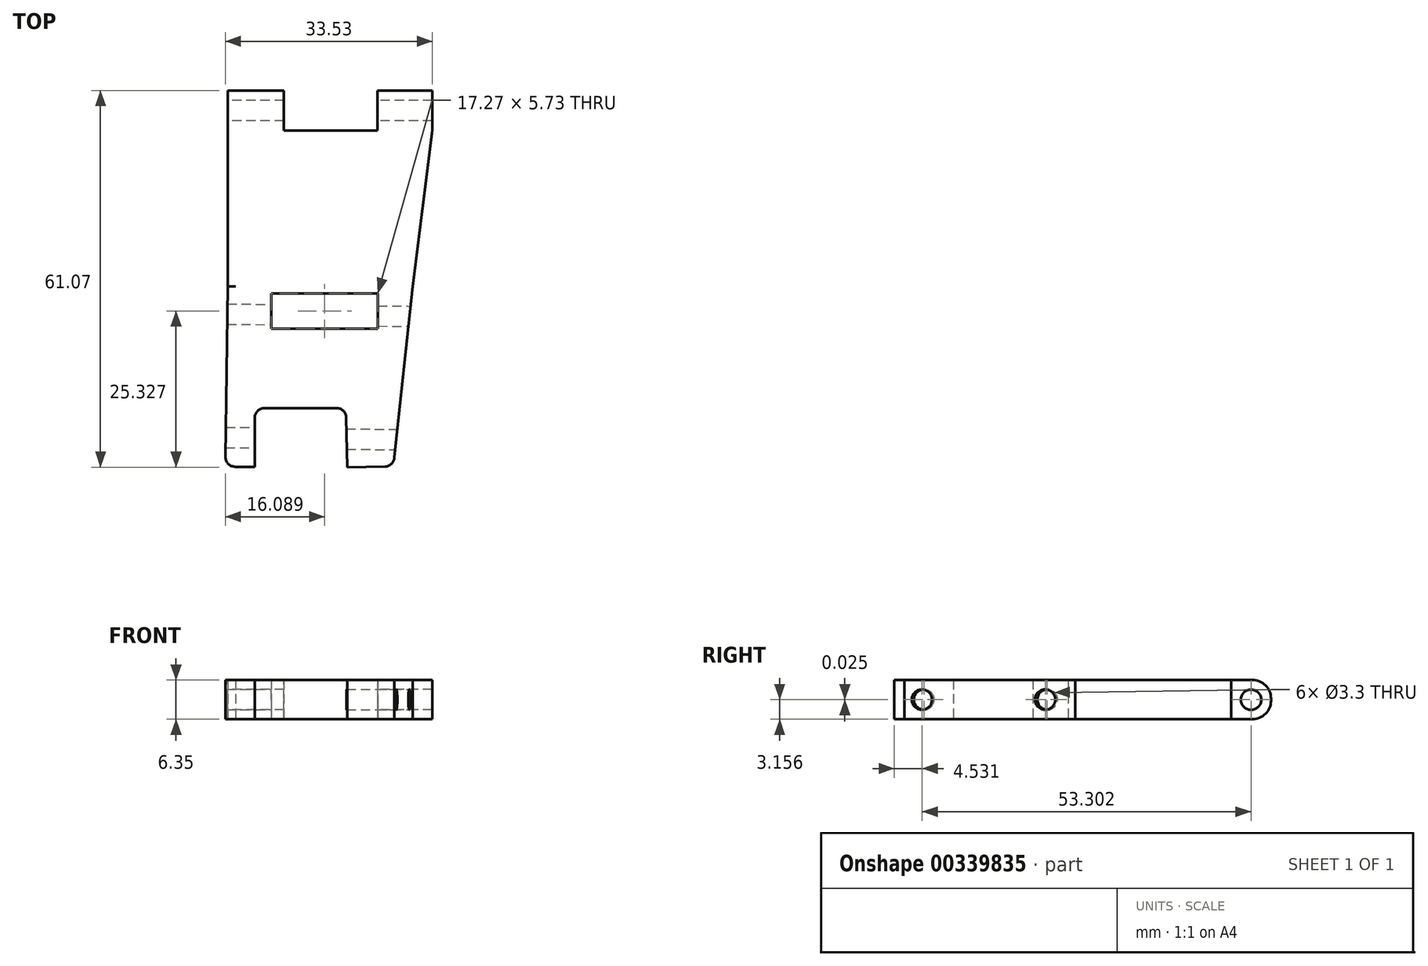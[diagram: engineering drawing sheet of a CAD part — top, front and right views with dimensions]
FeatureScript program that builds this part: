
annotation { "Feature Type Name" : "Feature", "Feature Type Description" : "" }
export const myFeature = defineFeature(function(context is Context, id is Id, definition is map)
    precondition{}
    {
        {
            var Q0;
            Q0=qCreatedBy(makeId("Top.planeOp"),FACE);
            var sketch = newSketch(context, id + "F0", { "sketchPlane" : qUnion([Q0])});
            skLineSegment(sketch, "E0.bottom", {"start": v(-49.27, 51.46) * mm, "end": v(-40.15, 51.46) * mm});
            skLineSegment(sketch, "E0.top", {"start": v(-49.27, 19.7) * mm, "end": v(-19.3, 19.7) * mm});
            skLineSegment(sketch, "E0.left", {"start": v(-49.27, 51.46) * mm, "end": v(-49.27, 19.7) * mm});
            skLineSegment(sketch, "E0.right", {"start": v(-16.1, 51.46) * mm, "end": v(-16.1, 45.01) * mm});
            skLineSegment(sketch, "E1", {"start": v(-40.15, 51.46) * mm, "end": v(-40.15, 45.01) * mm});
            skLineSegment(sketch, "E2", {"start": v(-40.15, 45.01) * mm, "end": v(-25, 45.01) * mm});
            skLineSegment(sketch, "E3", {"start": v(-25, 45.01) * mm, "end": v(-25, 51.46) * mm});
            skLineSegment(sketch, "E4", {"start": v(-25, 51.46) * mm, "end": v(-16.1, 51.46) * mm});
            skLineSegment(sketch, "E5", {"start": v(-16.1, 45.01) * mm, "end": v(-19.3, 19.7) * mm});
            skSolve(sketch);
        }
        {
            var Q0;
            Q0=makeQuery(id+"F0.imprint","IMPRINT",FACE,{"disambiguationData":[TD([[makeQuery(id+"F0.imprint","IMPRINT",EDGE,{"derivedFrom":sQuery(id+"F0.wireOp",EDGE,"E0.top")}),1.0]])]});
            extrude(context, id + "F1", {"entities" : qUnion([Q0]), "depth" : 6.35 * mm});
        }
        {
            var Q0;
            Q0=makeQuery(id+"F1.opExtrude","SWEPT_FACE",FACE,{"disambiguationData":[OSD([sQuery(id+"F0.wireOp",EDGE,"E0.right")])]});
            var sketch = newSketch(context, id + "F2", { "sketchPlane" : qUnion([Q0])});
            skCircle(sketch, "E6", {"center": v(48.22, 3.16) * mm, "radius": 1.5 * mm});
            skSolve(sketch);
        }
        {
            var Q0;
            Q0=sQuery(id+"F2.wireOp",VERTEX,"E6.center");
            var Q1;
            Q1=makeQuery(id+"F1.opExtrude","SWEPT_BODY",BODY,{"disambiguationData":[OSD([sQuery(id+"F0.wireOp",EDGE,"E0.top"),sQuery(id+"F0.wireOp",EDGE,"E0.left"),sQuery(id+"F0.wireOp",EDGE,"E0.bottom"),sQuery(id+"F0.wireOp",EDGE,"E1"),sQuery(id+"F0.wireOp",EDGE,"E2"),sQuery(id+"F0.wireOp",EDGE,"E3"),sQuery(id+"F0.wireOp",EDGE,"E0.right"),sQuery(id+"F0.wireOp",EDGE,"E5"),sQuery(id+"F0.wireOp",EDGE,"E4")])]});
            hole(context, id + "F3", {"style" : HoleStyle.SIMPLE, "endStyle" : HoleEndStyle.THROUGH, "standardTappedOrClearance" : lookupTablePath({ "standard" : "ISO", "fit" : "Normal", "size" : "M3", "type" : "Clearance" }), "standardBlindInLast" : lookupTablePath({ "fit" : "Standard", "standard" : "ISO", "size" : "M3", "type" : "Clearance" }), "holeDiameter" : 3.3 * mm, "isTappedThrough" : true, "tappedDepth" : 12.7 * mm, "tapClearance" : 3, "locations" : qUnion([Q0]), "scope" : qUnion([Q1]), "startStyle" : HoleStartStyle.PART});
        }
        {
            var Q0;
            Q0=makeQuery(id+"F1.opExtrude","CAP_EDGE",EDGE,{"disambiguationData":[OSD([sQuery(id+"F0.wireOp",EDGE,"E4")])],"isStart":true});
            var Q1;
            Q1=makeQuery(id+"F1.opExtrude","CAP_EDGE",EDGE,{"disambiguationData":[OSD([sQuery(id+"F0.wireOp",EDGE,"E4")])],"isStart":false});
            var Q2;
            Q2=makeQuery(id+"F1.opExtrude","CAP_EDGE",EDGE,{"disambiguationData":[OSD([sQuery(id+"F0.wireOp",EDGE,"E0.bottom")])],"isStart":true});
            var Q3;
            Q3=makeQuery(id+"F1.opExtrude","CAP_EDGE",EDGE,{"disambiguationData":[OSD([sQuery(id+"F0.wireOp",EDGE,"E0.bottom")])],"isStart":false});
            fillet(context, id + "F4", {"entities" : qUnion([Q0, Q1, Q2, Q3]), "radius" : 3 * mm, "tangentPropagation" : true, "allowEdgeOverflow" : false});
        }
        {
            var Q0;
            Q0=qCreatedBy(makeId("Top.planeOp"),FACE);
            var sketch = newSketch(context, id + "F5", { "sketchPlane" : qUnion([Q0])});
            skLineSegment(sketch, "E7", {"start": v(-49.63, 0) * mm, "end": v(-49.63, -7.95) * mm});
            skLineSegment(sketch, "E8", {"start": v(-44.88, -9.53) * mm, "end": v(-44.88, -1.59) * mm});
            skLineSegment(sketch, "E9", {"start": v(-48.05, -9.53) * mm, "end": v(-44.88, -9.53) * mm});
            skLineSegment(sketch, "E10", {"start": v(-29.9, -9.61) * mm, "end": v(-23.8, -9.5) * mm});
            skLineSegment(sketch, "E11", {"start": v(-43.29, 0) * mm, "end": v(-31.63, 0) * mm});
            skPoint(sketch, "E12.visualSharp", {"position": v(-26.3, 0) * mm});
            skPoint(sketch, "E13.visualSharp", {"position": v(-44.88, 0) * mm});
            skArc(sketch, "E13.filletArc", {"start": v(-43.29, 0) * mm, "mid": v(-44.41, -0.46) * mm, "end": v(-44.88, -1.59) * mm});
            skPoint(sketch, "E14.visualSharp", {"position": v(-49.63, -9.53) * mm});
            skArc(sketch, "E14.filletArc", {"start": v(-49.63, -7.95) * mm, "mid": v(-49.16, -9.06) * mm, "end": v(-48.05, -9.53) * mm});
            skPoint(sketch, "E15.visualSharp", {"position": v(-25.16, -9.53) * mm});
            skArc(sketch, "E15.filletArc", {"start": v(-23.8, -9.5) * mm, "mid": v(-22.7, -9.04) * mm, "end": v(-22.25, -7.95) * mm});
            skLineSegment(sketch, "E16", {"start": v(-19.3, 19.74) * mm, "end": v(-22.25, -7.95) * mm});
            skLineSegment(sketch, "E17", {"start": v(-19.3, 19.74) * mm, "end": v(-49.27, 19.7) * mm});
            skLineSegment(sketch, "E18", {"start": v(-49.27, 19.7) * mm, "end": v(-49.63, -7.95) * mm});
            skLineSegment(sketch, "E19", {"start": v(-29.9, -9.61) * mm, "end": v(-30.05, -1.55) * mm});
            skPoint(sketch, "E20.visualSharp", {"position": v(-30.08, 0) * mm});
            skArc(sketch, "E20.filletArc", {"start": v(-30.05, -1.55) * mm, "mid": v(-30.53, -0.45) * mm, "end": v(-31.63, 0) * mm});
            skLineSegment(sketch, "E21.bottom", {"start": v(-42.17, 18.58) * mm, "end": v(-24.9, 18.58) * mm});
            skLineSegment(sketch, "E21.top", {"start": v(-42.17, 12.85) * mm, "end": v(-24.9, 12.85) * mm});
            skLineSegment(sketch, "E21.left", {"start": v(-42.17, 18.58) * mm, "end": v(-42.17, 12.85) * mm});
            skLineSegment(sketch, "E21.right", {"start": v(-24.9, 18.58) * mm, "end": v(-24.9, 12.85) * mm});
            skSolve(sketch);
        }
        {
            var Q0;
            Q0=makeQuery(id+"F5.imprint","IMPRINT",FACE,{"disambiguationData":[TD([[makeQuery(id+"F5.imprint","IMPRINT",EDGE,{"derivedFrom":sQuery(id+"F5.wireOp",EDGE,"E8")}),1.0]])]});
            extrude(context, id + "F6", {"entities" : qUnion([Q0]), "operationType" : NewBodyOperationType.ADD, "depth" : 6.35 * mm});
        }
        {
            var Q0;
            Q0=makeQuery(id+"F6.opExtrude","SWEPT_FACE",FACE,{"disambiguationData":[OSD([sQuery(id+"F5.wireOp",EDGE,"E18")])]});
            var sketch = newSketch(context, id + "F7", { "sketchPlane" : qUnion([Q0])});
            skCircle(sketch, "E22", {"center": v(5.4, 3.18) * mm, "radius": 1.5 * mm});
            skPoint(sketch, "E23.start.orphan", {"position": v(8.58, 0) * mm});
            skPoint(sketch, "E24.start.orphan", {"position": v(2.23, 6.35) * mm});
            skSolve(sketch);
        }
        {
            var Q0;
            Q0=sQuery(id+"F7.wireOp",VERTEX,"E22.center");
            var Q1;
            Q1=makeQuery(id+"F1.opExtrude","SWEPT_BODY",BODY,{"disambiguationData":[OSD([sQuery(id+"F0.wireOp",EDGE,"E0.top"),sQuery(id+"F0.wireOp",EDGE,"E0.left"),sQuery(id+"F0.wireOp",EDGE,"E0.bottom"),sQuery(id+"F0.wireOp",EDGE,"E1"),sQuery(id+"F0.wireOp",EDGE,"E2"),sQuery(id+"F0.wireOp",EDGE,"E3"),sQuery(id+"F0.wireOp",EDGE,"E0.right"),sQuery(id+"F0.wireOp",EDGE,"E5"),sQuery(id+"F0.wireOp",EDGE,"E4")])]});
            hole(context, id + "F8", {"style" : HoleStyle.SIMPLE, "endStyle" : HoleEndStyle.THROUGH, "standardTappedOrClearance" : lookupTablePath({ "standard" : "ISO", "fit" : "Normal", "size" : "M3", "type" : "Clearance" }), "standardBlindInLast" : lookupTablePath({ "fit" : "Standard", "standard" : "ISO", "size" : "M3", "type" : "Clearance" }), "holeDiameter" : 3.3 * mm, "isTappedThrough" : true, "tappedDepth" : 12.7 * mm, "tapClearance" : 3, "locations" : qUnion([Q0]), "scope" : qUnion([Q1]), "startStyle" : HoleStartStyle.PART});
        }
        {
            var Q0;
            Q0=makeQuery(id+"F6.opExtrude","SWEPT_FACE",FACE,{"disambiguationData":[OSD([sQuery(id+"F5.wireOp",EDGE,"E18")])]});
            var sketch = newSketch(context, id + "F9", { "sketchPlane" : qUnion([Q0])});
            skCircle(sketch, "E25", {"center": v(-14.6, 3.18) * mm, "radius": 2 * mm});
            skSolve(sketch);
        }
        {
            var Q0;
            Q0=sQuery(id+"F9.wireOp",VERTEX,"E25.center");
            var Q1;
            Q1=makeQuery(id+"F1.opExtrude","SWEPT_BODY",BODY,{"disambiguationData":[OSD([sQuery(id+"F0.wireOp",EDGE,"E0.top"),sQuery(id+"F0.wireOp",EDGE,"E0.left"),sQuery(id+"F0.wireOp",EDGE,"E0.bottom"),sQuery(id+"F0.wireOp",EDGE,"E1"),sQuery(id+"F0.wireOp",EDGE,"E2"),sQuery(id+"F0.wireOp",EDGE,"E3"),sQuery(id+"F0.wireOp",EDGE,"E0.right"),sQuery(id+"F0.wireOp",EDGE,"E5"),sQuery(id+"F0.wireOp",EDGE,"E4")])]});
            hole(context, id + "F10", {"style" : HoleStyle.SIMPLE, "endStyle" : HoleEndStyle.THROUGH, "standardTappedOrClearance" : lookupTablePath({ "standard" : "ISO", "fit" : "Normal", "size" : "M3", "type" : "Clearance" }), "standardBlindInLast" : lookupTablePath({ "fit" : "Standard", "standard" : "ISO", "size" : "M3", "type" : "Clearance" }), "holeDiameter" : 3.3 * mm, "isTappedThrough" : true, "tappedDepth" : 12.7 * mm, "tapClearance" : 3, "locations" : qUnion([Q0]), "scope" : qUnion([Q1]), "startStyle" : HoleStartStyle.PART});
        }
    });
